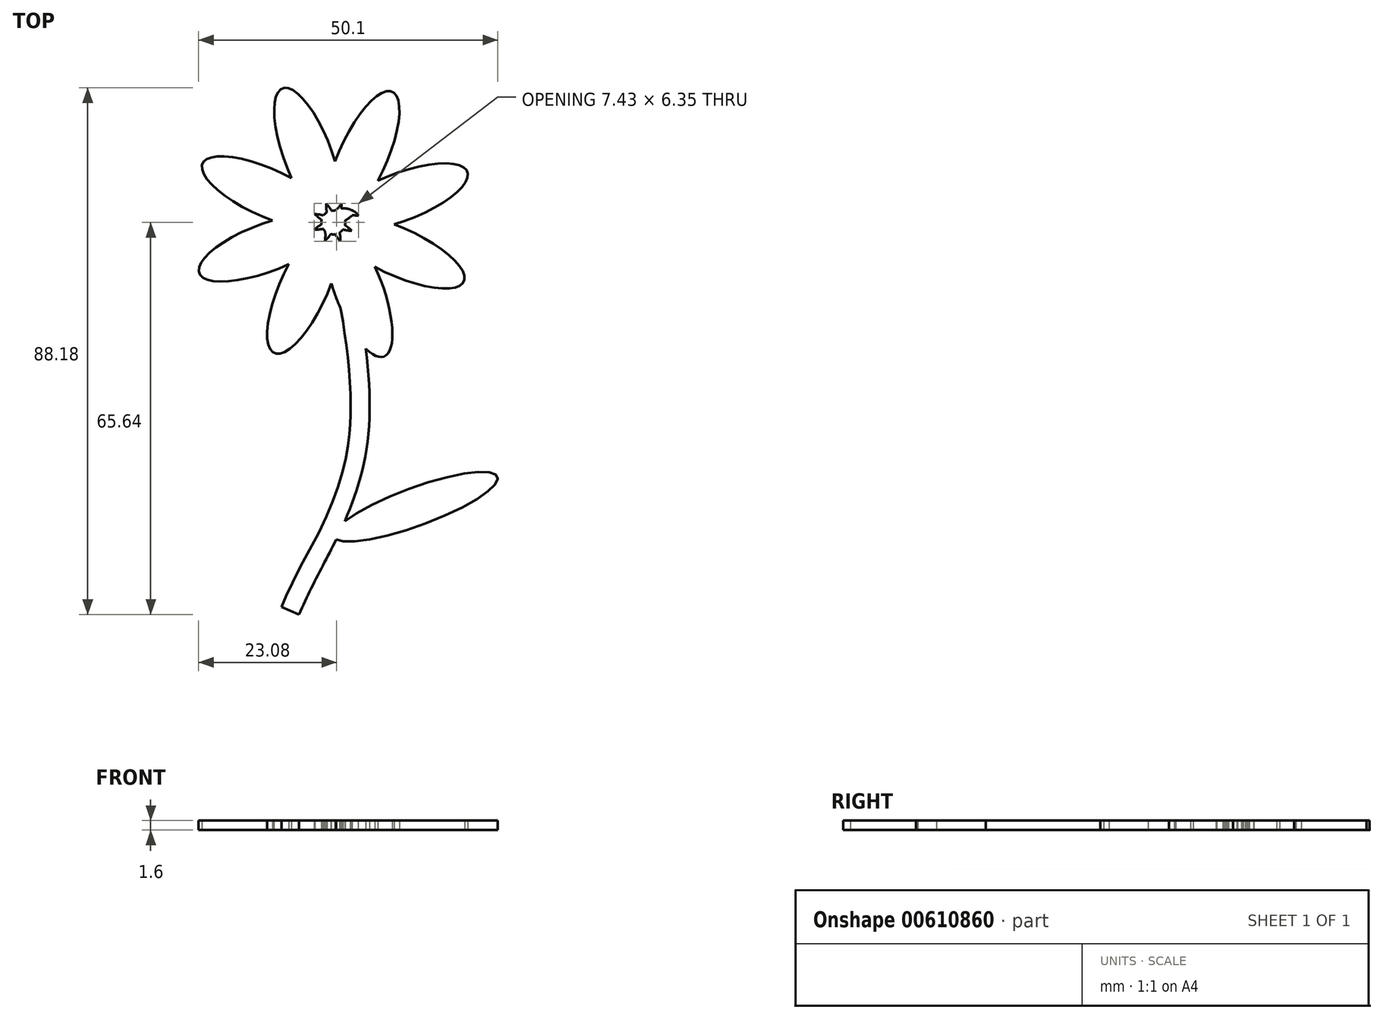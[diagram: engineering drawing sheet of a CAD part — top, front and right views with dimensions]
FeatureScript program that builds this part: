
annotation { "Feature Type Name" : "Feature", "Feature Type Description" : "" }
export const myFeature = defineFeature(function(context is Context, id is Id, definition is map)
    precondition{}
    {
        {
            var Q0;
            Q0=qCreatedBy(makeId("Top.planeOp"),FACE);
            var sketch = newSketch(context, id + "F0", { "sketchPlane" : qUnion([Q0])});
            skFitSpline(sketch, "E0", {"points": [v(27.7, -18.04) * mm, v(39.48, 14.7) * mm, v(35.2, 46.7) * mm], "startDerivative": vector(25.02, 59.53) * mm, "endDerivative": vector(3.15, -7.17) * mm});
            skFitSpline(sketch, "E1.0", {"points": [v(24.75, -16.8) * mm, v(25.85, -14.18) * mm, v(28.35, -9.28) * mm, v(31.44, -3.43) * mm, v(33.53, 1.45) * mm, v(34.83, 5.3) * mm, v(35.63, 8.75) * mm, v(36.06, 11.73) * mm, v(36.23, 13.68) * mm, v(36.3, 15.32) * mm, v(36.33, 17) * mm, v(36.29, 19.2) * mm, v(36.13, 21.93) * mm, v(35.87, 24.7) * mm, v(35.54, 27.48) * mm, v(35.16, 30.21) * mm, v(34.73, 32.86) * mm, v(34.28, 35.38) * mm, v(33.9, 37.34) * mm, v(33.6, 38.8) * mm, v(33.4, 39.85) * mm, v(33.18, 40.82) * mm, v(32.99, 41.73) * mm, v(32.8, 42.57) * mm, v(32.63, 43.33) * mm, v(32.5, 43.9) * mm, v(32.4, 44.3) * mm, v(32.34, 44.6) * mm, v(32.28, 44.86) * mm, v(32.23, 45.1) * mm, v(32.18, 45.32) * mm, v(32.14, 45.49) * mm, v(32.12, 45.61) * mm, v(32.1, 45.7) * mm, v(32.08, 45.78) * mm, v(32.06, 45.87) * mm, v(32.05, 45.95) * mm, v(32.03, 46.03) * mm, v(32.02, 46.1) * mm, v(32, 46.18) * mm, v(32, 46.23) * mm, v(32, 46.3) * mm, v(31.98, 46.38) * mm, v(31.97, 46.49) * mm, v(31.97, 46.6) * mm, v(31.97, 46.73) * mm, v(31.97, 46.85) * mm, v(31.98, 47.01) * mm, v(32, 47.22) * mm, v(32.05, 47.5) * mm, v(32.16, 47.86) * mm, v(32.33, 48.23) * mm, v(32.53, 48.56) * mm, v(32.83, 48.95) * mm, v(33.28, 49.35) * mm, v(33.9, 49.7) * mm, v(34.62, 49.93) * mm, v(35.34, 49.96) * mm, v(35.95, 49.86) * mm, v(36.43, 49.7) * mm, v(36.91, 49.45) * mm, v(37.29, 49.16) * mm, v(37.54, 48.9) * mm, v(37.7, 48.7) * mm, v(37.82, 48.55) * mm, v(37.9, 48.43) * mm, v(37.95, 48.34) * mm, v(38, 48.24) * mm, v(38.06, 48.14) * mm, v(38.1, 48.05) * mm, v(38.12, 48) * mm, v(38.13, 47.98) * mm]});
            skCircle(sketch, "E2", {"center": v(33.42, 47.6) * mm, "radius": 2 * mm});
            skLineSegment(sketch, "E3", {"start": v(31.6, 48.42) * mm, "end": v(22.48, 52.54) * mm});
            skPoint(sketch, "E4", {"position": v(31.43, 47.44) * mm});
            skPoint(sketch, "E5.MirrorP", {"position": v(32.22, 49.2) * mm});
            skEllipticalArc(sketch, "E6", {});
            skPoint(sketch, "E7.center", {"position": v(0, 0) * mm});
            skEllipticalArc(sketch, "E8.1.0", {});
            skEllipticalArc(sketch, "E8.2.0", {});
            skEllipticalArc(sketch, "E8.3.0", {});
            skEllipticalArc(sketch, "E8.4.0", {});
            skEllipticalArc(sketch, "E8.5.0", {});
            skEllipticalArc(sketch, "E8.6.0", {});
            skLineSegment(sketch, "E9", {"start": v(24.75, -16.8) * mm, "end": v(27.7, -18.04) * mm});
            skPoint(sketch, "E10", {"position": v(47.22, 0) * mm});
            skEllipticalArc(sketch, "E11", {});
            skEllipticalArc(sketch, "E12.trimOffspring", {});
            skEllipticalArc(sketch, "E13.trimOffspring", {});
            skEllipticalArc(sketch, "E14.0.7.0", {});
            const initialGuessF0  = {"E6": [0.022483060798572357, 0.052537843462137315, 0.9114105490091753, -0.4114982517032042, 0.012, 0.004, 0.4311310920971165, 5.852054215082472], "E8.1.0": [0.022194733980181423, 0.0433579679366157, 0.9354377838750865, 0.3534913754235979, 0.012, 0.004, 0.43113109209711586, 5.85205421508247], "E8.2.0": [0.028482008366244017, 0.03666293785358876, 0.41149825170320425, 0.9114105490091754, 0.012, 0.004, 0.4311310920971169, 5.061191727571062], "E8.3.0": [0.037661883891765634, 0.03637461103519783, -0.3534913754235979, 0.9354377838750866, 0.012, 0.004, 0.4311310920971159, 5.852054215082471], "E8.4.0": [0.044356913974792564, 0.042661885421260426, -0.9114105490091753, 0.4114982517032043, 0.012, 0.004, 0.4311310920971145, 0.6435011087932847], "E8.5.0": [0.04464524079318351, 0.05184176094678204, -0.9354377838750866, -0.3534913754235978, 0.012, 0.004, 0.4311310920971141, 5.852054215082471], "E8.6.0": [0.0383579664071209, 0.05853679102980898, -0.41149825170320414, -0.9114105490091753, 0.012, 0.004, 0.431131092097117, 5.852054215082472], "E11": [0.047218208778905174, 0, -0.9388011260873479, -0.3444596430020903, 0.014609452320641805, 0.0032, 0.17600770532982, 5.67319197261525], "E12.trimOffspring": [0.028482008366244014, 0.036662937853588776, 0.41149825170320425, 0.9114105490091754, 0.012, 0.004, 5.639684198386302, 5.852054215082469], "E13.trimOffspring": [0.04435691397479256, 0.04266188542126044, -0.9114105490091755, 0.4114982517032042, 0.012, 0.004, 0.8569773812307843, 5.852054215082471], "E14.0.7.0": [0.029178090881599283, 0.05882511784819991, 0.35349137542359765, -0.9354377838750865, 0.012, 0.004, 0.4311310920971155, 5.852054215082471]};
            skSetInitialGuess(sketch, initialGuessF0);
            skSolve(sketch);
        }
        {
            var Q0;
            Q0 = qSketchRegion(id + "F0", true);
            extrude(context, id + "F1", {"entities" : qUnion([Q0]), "depth" : 1.6 * mm, "offsetDistance" : 25 * mm});
        }
    });
